# Revit family: ledbollard-leo-p_l1000-8w-830_840-fr_703000005800_66e0
name_source: partatom
category: Lighting Fixtures
units: mm (PartAtom-declared; Revit-internal decimal feet)

## family parameters
Cut with Voids When Loaded = No
Host = Face
Light Source = No
Part Type = Normal
Room Calculation Point = No
Round Connector Dimension = Use Diameter
Shared = No

## types (1)
- LEDBollard-Leo-P L1000-8W-830/840-FR (1 x LED, 530 lm, 4000)
    Apparent Load = 8 VA
    Approval mark = CE, ENEC
    CIE Flux Codes = 12 36 66 48 80
    Color Rendering = 80
    Color Temperature = 4000
    Control Gear = Electronic ballast
    Default Elevation = 1800 mm
    Description = Bollard / Wall Light Leo mm-8W-530lm-3/4000K-320°-Black-IP65
    Frequency = 60 Hz
    Height = 1000 mm  [stored 3.28084 ft]
    Lamp = 1 x LED
    Lamp Light Flux = 530 lm
    Lamp count = 1
    Length = 100 mm  [stored 0.328084 ft]
    Luminous efficacy = 53 lm/W
    Manufacturer = OPPLE
    ModVariant = No
    Model = 703000005800
    Number of Poles = 1
    OnlyDefault = Yes
    Power Factor = 1
    Product Name = LEDBollard-Leo-P L1000-8W-830/840-FR
    Product group = Bollard / pole mounted luminaires
    ProductGroupID = 31
    Protection Class = Protection class I
    Protection Degree = IP 65
    RLX_Detail_Level = 1
    RLX_Emergency_Light_Flux = 0 lm
    RLX_Emergency_Type = 0
    RLX_Emergency_Type_DB = No
    RlxData = <blob elided: 103165 chars, md5=120fc529>
    Socket = socket
    Standby Power = 0 W
    System Light Flux = 422 lm
    System Power = 8 W
    Type Comments = Product without accessories
    Type Image = web_leo_boll_fr.jpg
    URL = http://relux.com
    VarID = ---
    Voltage = 230 V
    Voltage Range = 220-240 V
    Weight = 0.00 kg
    Width = 100 mm  [stored 0.328084 ft]

note: [stored X ft] marks values corroborated as IEEE doubles in the binary element streams (Revit-internal decimal feet)

## geometry (parser evidence)
native form markers: Blend x4, Sweep x13
no freeform markers — native parametric forms only
